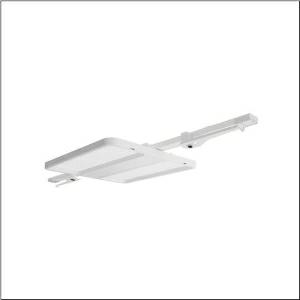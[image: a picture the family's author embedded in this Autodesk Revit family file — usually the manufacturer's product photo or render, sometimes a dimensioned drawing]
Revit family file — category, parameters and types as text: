
# Revit family: highbay_11_fur_modario_r__tragschiene_midi_51hn12da6lma_0648
name_source: partatom
category: Lighting Fixtures
units: mm (PartAtom-declared; Revit-internal decimal feet)

## family parameters
Cut with Voids When Loaded = No
Host = Face
Light Source = No
Part Type = Normal
Room Calculation Point = No
Round Connector Dimension = Use Diameter
Shared = No

## types (1)
- --- (1 x LED, 26540 lm, 146.7 W, 6500K)
    Apparent Load = 147 VA
    CIE Flux Codes = 87 98 100 100 100
    Color Rendering = 80
    Color Temperature = 6500K
    Default Elevation = 1800 mm
    Description = high bay luminaire Highbay 11 for Modario® trunking rail midi; direct symmetric wide distribution, light control with lens of PMMA; UGR ≤ 22 (X = 4H | Y = 8H | S = 0.25H | reflection values 70/50/20); luminous flux: 26.540lm; light colour: 865, colour temperature: 6500K, MacAdam ≤ 2 SDCM (initial), colour rendering: CRI > 80; luminous efficacy: 180,9lm/W; rated service life: 100.000h (L95/B50) at AT= 25°C; control: DALI 2; luminaire connection: plug, 5-pole, with phase selectionmains connection: 230..240V, AC 50/60Hz; connected load: 146,7W; protection rating (complete): IP64; insulation class (complete): insulation class I (protective earthing); protection symbol: D; impact resistance: IK07; certification: CE, ENEC, VDE, UKCA; internal wiring halogen-free; luminaire corresponds to IFS (International Featured Standards) requirements for safety and quality in the food industry; LABS conformity tested according to VDMA 24364:2018-05; housing frame of high-performance plastic PA6, matt traffic white (RAL 9016); cover of PMMA; fixing on rail side of steel, galvanised, white; blank cover of PC, traffic white (RAL 9016); dimension (LxWxH): 1.195 x 442 x 72mm; permissible operating ambient temperature: -40..+50°C (reducing of maximum allowable ambient temperature of 5°C with ceiling mounting); packaging unit: 1 piece
    Height = 72 mm  [stored 0.23622 ft]
    Lamp = 1 x LED
    Lamp Light Flux = 26540 lm
    Lamp Power = 146.7 W
    Lamp count = 1
    Length = 474 mm
    Luminous efficacy = 181 lm/W
    Manufacturer = Siteco
    ModVariant = No
    Model = 51HN12DA6LMA
    Mounting Place = Ceiling
    Mounting Type = Pendant
    Number of Poles = 1
    OnlyDefault = Yes
    Power Factor = 1
    Product Name = Highbay 11 für Modario® Tragschiene midi
    Product group = high bay luminaire
    ProductGroupID = 901
    Protection Class = Protection class I
    Protection Degree = IP 64
    RLX_Detail_Level = 1
    RLX_Emergency_Light_Flux = 0 lm
    RLX_Emergency_Type = 0
    RLX_Emergency_Type_DB = No
    RlxData = <blob elided: 18125 chars, md5=ebd247e0>
    Socket = socket
    Standby Power = 0 W
    System Light Flux = 26539 lm
    System Power = 147 W
    Type Comments = factory setting: luminous flux: 100 % | dim-lin: 254 | 661 mA
    Type Image = l_1363266.jpg
    URL = http://relux.com
    VarID = @adj_007851
    Voltage = 0 V
    Weight = 0.00 kg
    Width = 442 mm

note: [stored X ft] marks values corroborated as IEEE doubles in the binary element streams (Revit-internal decimal feet)

## geometry (parser evidence)
native form markers: Blend x4, Sweep x10
no freeform markers — native parametric forms only
